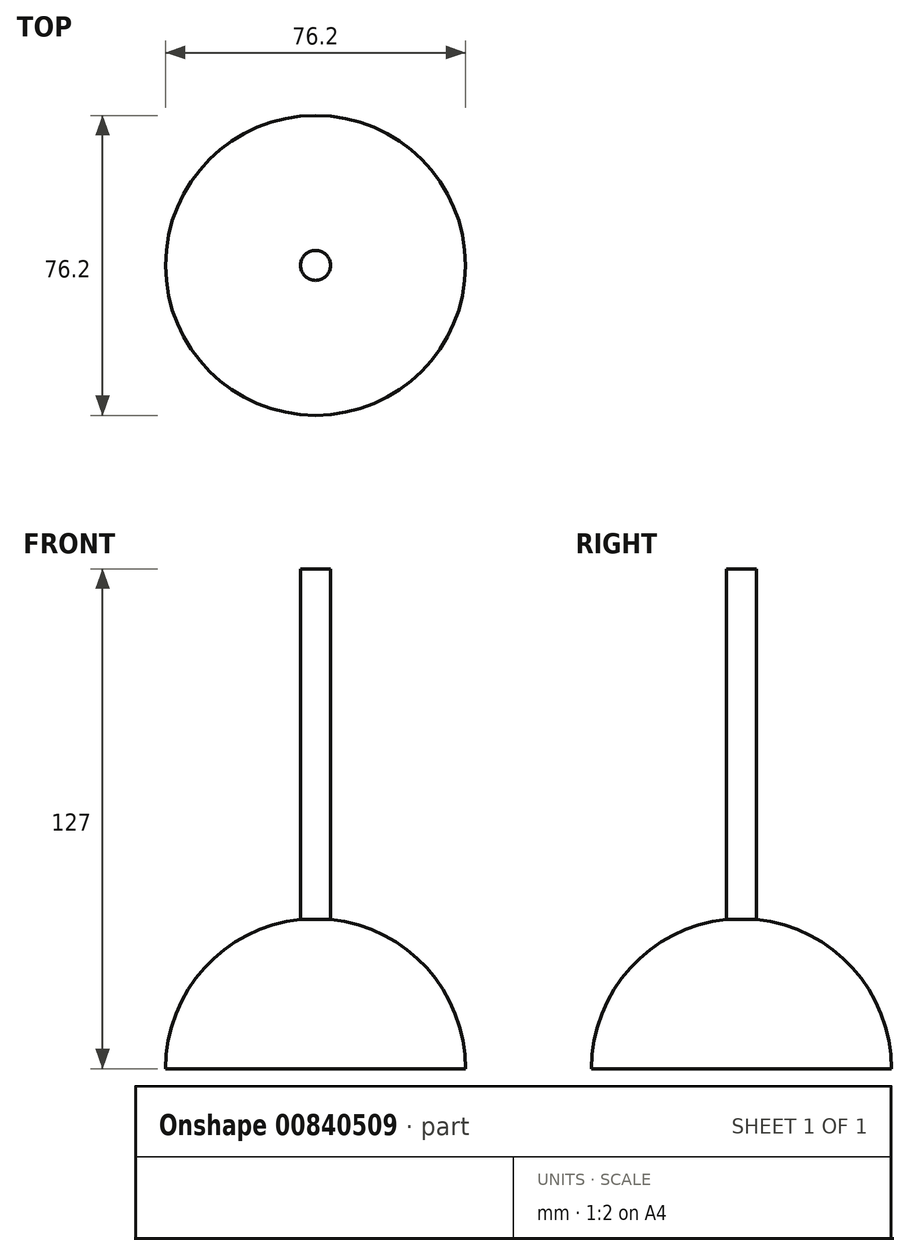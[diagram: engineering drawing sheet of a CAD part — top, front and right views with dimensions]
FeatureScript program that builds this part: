
annotation { "Feature Type Name" : "Feature", "Feature Type Description" : "" }
export const myFeature = defineFeature(function(context is Context, id is Id, definition is map)
    precondition{}
    {
        {
            var Q0;
            Q0=qCreatedBy(makeId("Top.planeOp"),FACE);
            var sketch = newSketch(context, id + "F0", { "sketchPlane" : qUnion([Q0])});
            skLineSegment(sketch, "E0", {"start": v(0, 0) * mm, "end": v(0, 76.2) * mm});
            skArc(sketch, "E1", {"start": v(0, 0) * mm, "mid": v(38.1, 38.1) * mm, "end": v(0, 76.2) * mm});
            skSolve(sketch);
        }
        {
            var Q0;
            Q0=makeQuery(id+"F0.imprint","IMPRINT",FACE,{"disambiguationData":[TD([[makeQuery(id+"F0.imprint","IMPRINT",EDGE,{"derivedFrom":sQuery(id+"F0.wireOp",EDGE,"E0")}),-1.0]])]});
            var Q1;
            Q1=sQuery(id+"F0.wireOp",EDGE,"E0");
            revolve(context, id + "F1", {"surfaceOperationType" : NewSurfaceOperationType.NEW, "entities" : qUnion([Q0]), "axis" : qUnion([Q1]), "revolveType" : RevolveType.ONE_DIRECTION, "oppositeDirection" : true, "angle" : 180 * degree});
        }
        {
            var Q0;
            Q0=makeQuery(id+"F1.opRevolve","CAP_FACE",FACE,{"disambiguationData":[OSD([sQuery(id+"F0.wireOp",EDGE,"E0"),sQuery(id+"F0.wireOp",EDGE,"E1")])],"isStart":true});
            var sketch = newSketch(context, id + "F2", { "sketchPlane" : qUnion([Q0])});
            skCircle(sketch, "E2", {"center": v(0, -38.1) * mm, "radius": 3.8 * mm});
            skSolve(sketch);
        }
        {
            var Q0;
            Q0=makeQuery(id+"F2.imprint","IMPRINT",FACE,{"disambiguationData":[TD([[makeQuery(id+"F2.imprint","IMPRINT",EDGE,{"derivedFrom":sQuery(id+"F2.wireOp",EDGE,"E2")}),1.0]])]});
            extrude(context, id + "F3", {"entities" : qUnion([Q0]), "operationType" : NewBodyOperationType.ADD, "oppositeDirection" : true, "depth" : 127 * mm, "offsetDistance" : 25.4 * mm});
        }
    });
